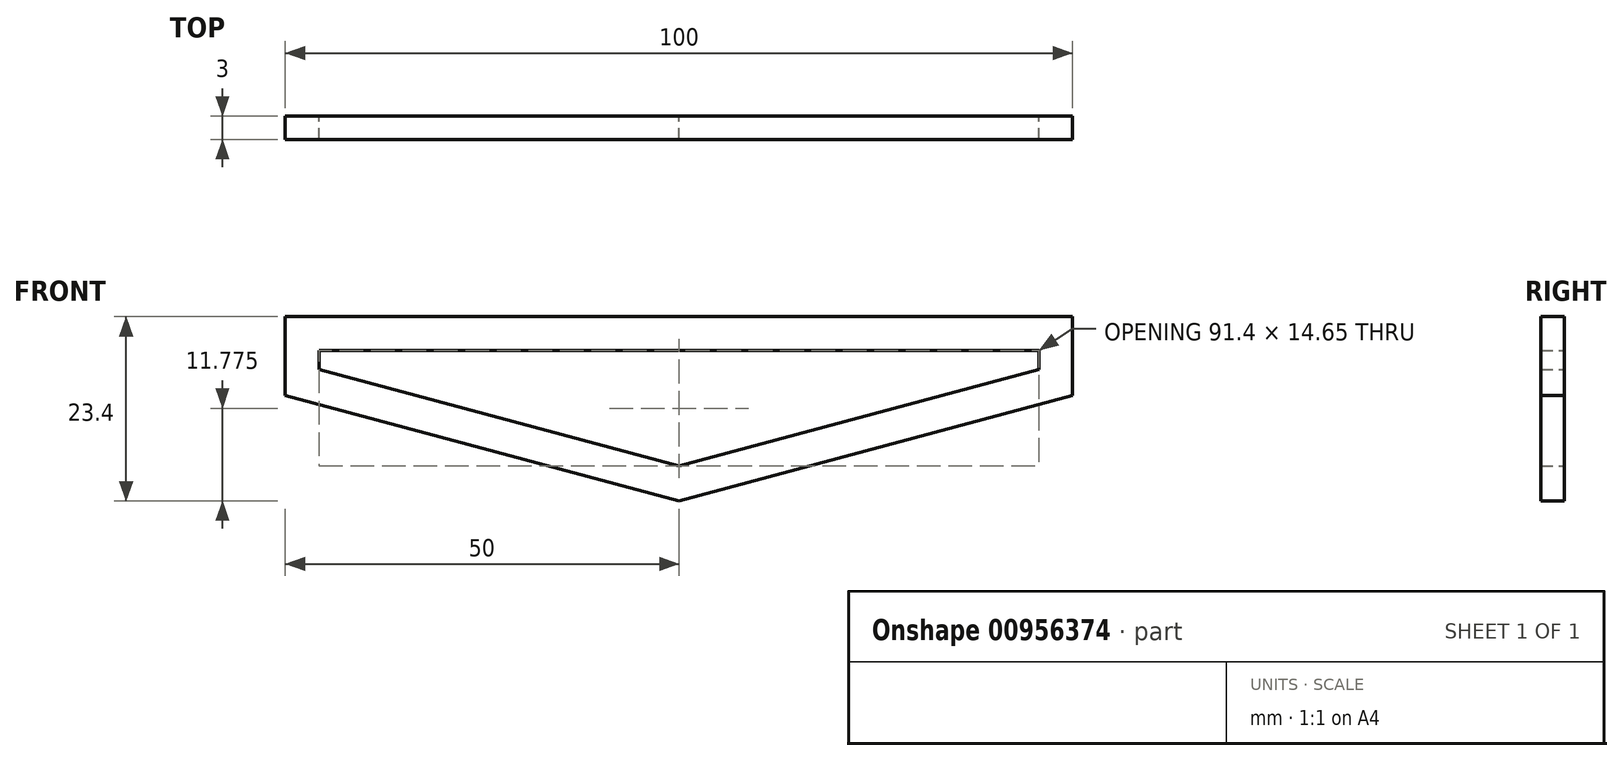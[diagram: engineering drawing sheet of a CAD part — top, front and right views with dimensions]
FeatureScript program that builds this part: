
annotation { "Feature Type Name" : "Feature", "Feature Type Description" : "" }
export const myFeature = defineFeature(function(context is Context, id is Id, definition is map)
    precondition{}
    {
        {
            var Q0;
            Q0=qCreatedBy(makeId("Front.planeOp"),FACE);
            var sketch = newSketch(context, id + "F0", { "sketchPlane" : qUnion([Q0])});
            skLineSegment(sketch, "E0", {"start": v(-50, 13.4) * mm, "end": v(0, 0) * mm});
            skLineSegment(sketch, "E1", {"start": v(0, 0) * mm, "end": v(-21.74, 0) * mm, "construction": true});
            skLineSegment(sketch, "E2", {"start": v(-50, 13.4) * mm, "end": v(-50, 23.4) * mm});
            skLineSegment(sketch, "E3", {"start": v(-50, 23.4) * mm, "end": v(0, 23.4) * mm});
            skLineSegment(sketch, "E4", {"start": v(0, 0) * mm, "end": v(0, 38.2) * mm, "construction": true});
            skLineSegment(sketch, "E5.0", {"start": v(-45.7, 19.1) * mm, "end": v(0, 19.1) * mm});
            skLineSegment(sketch, "E5.1", {"start": v(-45.7, 16.7) * mm, "end": v(-45.7, 19.1) * mm});
            skLineSegment(sketch, "E5.2", {"start": v(-45.7, 16.7) * mm, "end": v(0, 4.45) * mm});
            skLineSegment(sketch, "E6.MirrorCS", {"start": v(50, 13.4) * mm, "end": v(0, 0) * mm});
            skLineSegment(sketch, "E7.MirrorCS", {"start": v(45.7, 16.7) * mm, "end": v(0, 4.45) * mm});
            skLineSegment(sketch, "E8.MirrorCS", {"start": v(45.7, 16.7) * mm, "end": v(45.7, 19.1) * mm});
            skLineSegment(sketch, "E9.MirrorCS", {"start": v(45.7, 19.1) * mm, "end": v(0, 19.1) * mm});
            skLineSegment(sketch, "E10.MirrorCS", {"start": v(50, 23.4) * mm, "end": v(0, 23.4) * mm});
            skLineSegment(sketch, "E11.MirrorCS", {"start": v(50, 13.4) * mm, "end": v(50, 23.4) * mm});
            skSolve(sketch);
        }
        {
            var Q0;
            Q0 = qSketchRegion(id + "F0", true);
            extrude(context, id + "F1", {"entities" : qUnion([Q0]), "depth" : 3 * mm, "offsetDistance" : 25 * mm});
        }
    });
